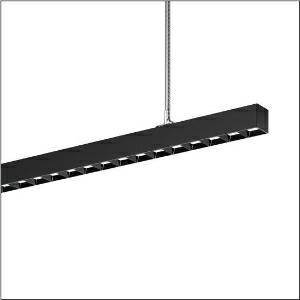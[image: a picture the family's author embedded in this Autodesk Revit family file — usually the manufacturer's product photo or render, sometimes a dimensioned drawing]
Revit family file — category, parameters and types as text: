
# Revit family: silica_r__21_51mx31dc3dbb_16a7
name_source: partatom
category: Lighting Fixtures
units: mm (PartAtom-declared; Revit-internal decimal feet)

## family parameters
Cut with Voids When Loaded = No
Host = Face
Light Source = No
Part Type = Normal
Room Calculation Point = No
Round Connector Dimension = Use Diameter
Shared = No

## types (1)
- --- (1 x LED, 18230 lm, 113.3 W, 3000K)
    Apparent Load = 113 VA
    CIE Flux Codes = 87 99 100 59 100
    Color Rendering = 80
    Color Temperature = 3000K
    Default Elevation = 1800 mm
    Description = Silica® 21, office luminaire, primary light control with darklight reflector, of PMMA, black, CAT 2 (L<= 3000cd/m²), light emission: direct/indirect distribution, primary light characteristic: symmetric, installation type: suspended mounting, LED, rated luminous flux: 18.230lm, luminous efficacy: 161lm/W, light colour: 830, colour temperature: 3000K, with terminal, 3+2-pole, max. 2.5mm², mains connection: 220..240V, AC, 50/60Hz, rated input power: 113.3W, luminaire housing, of aluminium, jet black (RAL 9005), length: 3.004mm, width: 53mm, height: 53mm, protection rating (complete): IP20, insulation class (complete): insulation class I (protective earthing), certification: CE, permissible operating ambient temperature: 0..+35°C, standard: EN 50419, packaging unit: 1 piece
    Height = 53 mm
    Lamp = 1 x LED
    Lamp Light Flux = 18230 lm
    Lamp Power = 113.3 W
    Lamp count = 1
    Length = 3004 mm
    Luminous efficacy = 161 lm/W
    Manufacturer = Siteco
    ModVariant = No
    Model = 51MX31DC3DBB
    Mounting Place = Ceiling
    Mounting Type = Pendant
    Number of Poles = 1
    OnlyDefault = Yes
    Power Factor = 1
    Product Name = Silica® 21
    Product group = office luminaire | ceiling pendant
    ProductGroupID = 905
    Protection Class = Protection class I
    Protection Degree = IP 20
    RLX_Detail_Level = 1
    RlxData = <blob elided: 66961 chars, md5=b75b0d22>
    Socket = socket
    Standby Power = 0 W
    System Light Flux = 18230 lm
    System Power = 113 W
    Type Comments = factory setting: luminous flux: 100 % | dim-lin: 254 | 392 mA
    Type Image = l_1251718.jpg
    URL = http://relux.com
    VarID = @adj_030119
    Voltage = 0 V
    Weight = 0.00 kg
    Width = 53 mm

## geometry (parser evidence)
native form markers: Blend x4, Sweep x13
no freeform markers — native parametric forms only
